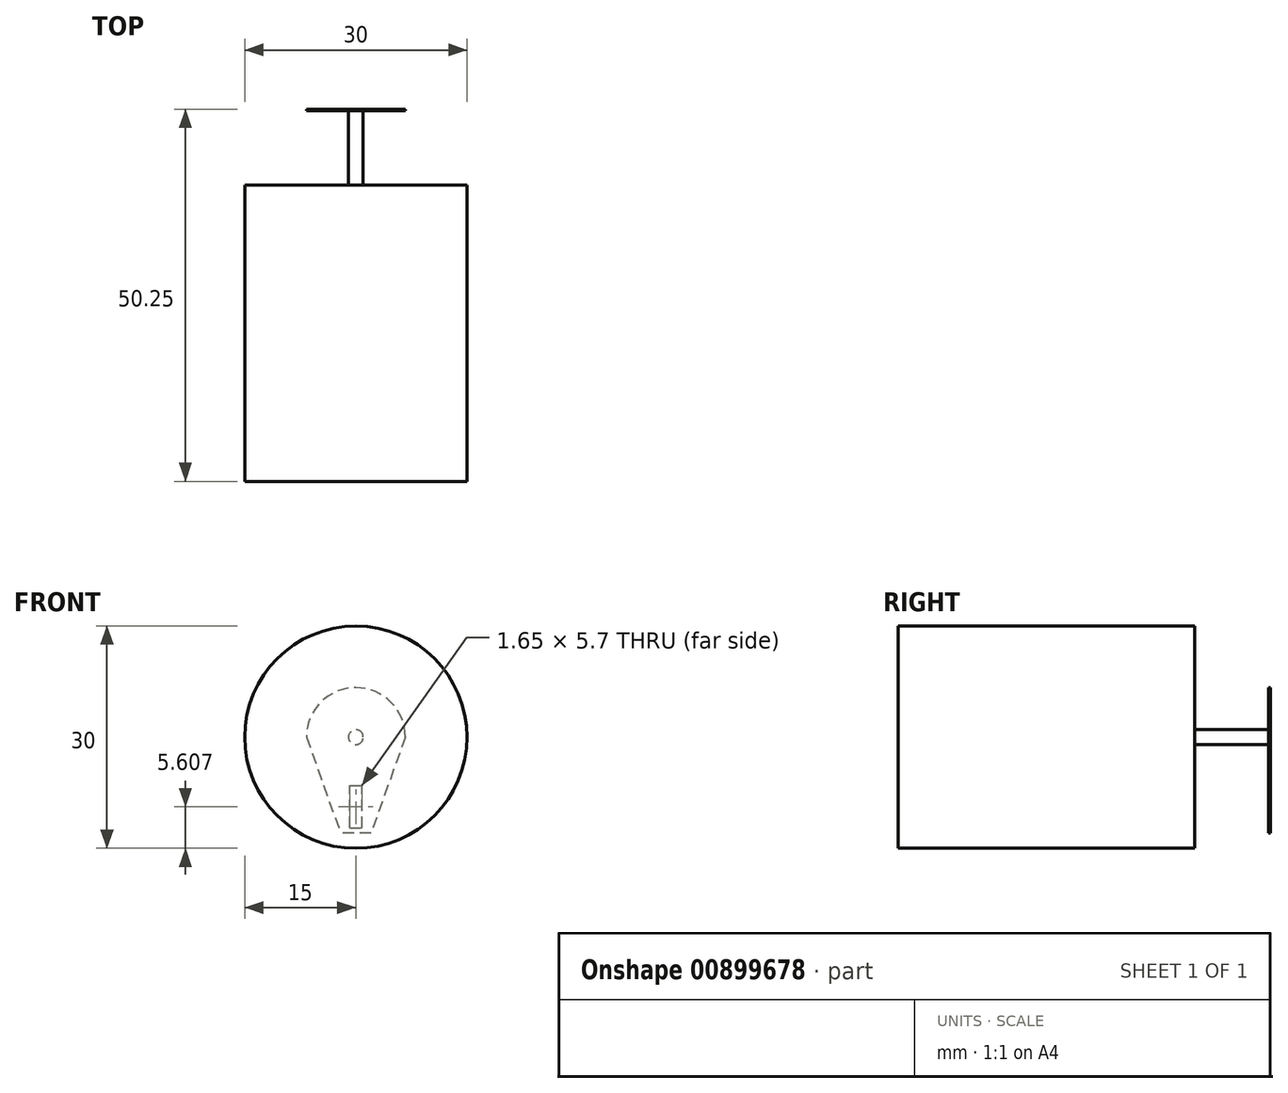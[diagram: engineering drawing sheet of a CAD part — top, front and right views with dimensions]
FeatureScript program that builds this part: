
annotation { "Feature Type Name" : "Feature", "Feature Type Description" : "" }
export const myFeature = defineFeature(function(context is Context, id is Id, definition is map)
    precondition{}
    {
        {
            var Q0;
            Q0=qCreatedBy(makeId("Front.planeOp"),FACE);
            var sketch = newSketch(context, id + "F0", { "sketchPlane" : qUnion([Q0])});
            skCircle(sketch, "E0", {"center": v(0, 0) * mm, "radius": 15 * mm});
            skSolve(sketch);
        }
        {
            var Q0;
            Q0=makeQuery(id+"F0.imprint","IMPRINT",FACE,{"disambiguationData":[TD([[makeQuery(id+"F0.imprint","IMPRINT",EDGE,{"derivedFrom":sQuery(id+"F0.wireOp",EDGE,"E0")}),1.0]])]});
            extrude(context, id + "F1", {"entities" : qUnion([Q0]), "depth" : 40 * mm, "offsetDistance" : 25.4 * mm});
        }
        {
            var Q0;
            Q0=makeQuery(id+"F1.opExtrude","CAP_FACE",FACE,{"disambiguationData":[OSD([sQuery(id+"F0.wireOp",EDGE,"E0")])],"isStart":true});
            var sketch = newSketch(context, id + "F2", { "sketchPlane" : qUnion([Q0])});
            skCircle(sketch, "E1", {"center": v(0, 0) * mm, "radius": 5 * mm});
            skCircle(sketch, "E2", {"center": v(0, 0) * mm, "radius": 1 * mm});
            skSolve(sketch);
        }
        {
            var Q0;
            Q0=makeQuery(id+"F2.imprint","IMPRINT",FACE,{"disambiguationData":[TD([[makeQuery(id+"F2.imprint","IMPRINT",EDGE,{"derivedFrom":sQuery(id+"F2.wireOp",EDGE,"E2")}),1.0]])]});
            extrude(context, id + "F3", {"entities" : qUnion([Q0]), "operationType" : NewBodyOperationType.ADD, "depth" : 10 * mm, "offsetDistance" : 25.4 * mm});
        }
        {
            var Q0;
            Q0=makeQuery(id+"F1.opExtrude","CAP_FACE",FACE,{"disambiguationData":[OSD([sQuery(id+"F0.wireOp",EDGE,"E0")])],"isStart":true});
            var sketch = newSketch(context, id + "F4", { "sketchPlane" : qUnion([Q0])});
            skSolve(sketch);
        }
        {
            var Q0;
            Q0=makeQuery(id+"F4.imprint","IMPRINT",FACE,{"disambiguationData":[TD([[makeQuery(id+"F4.imprint","IMPRINT",EDGE,{"derivedFrom":makeQuery(id+"F1.opExtrude","CAP_EDGE",EDGE,{"disambiguationData":[OSD([sQuery(id+"F0.wireOp",EDGE,"E0")])],"isStart":true})}),-1.0]])]});
            var sketch = newSketch(context, id + "F5", { "sketchPlane" : qUnion([Q0])});
            skLineSegment(sketch, "E3", {"start": v(0, -14.98) * mm, "end": v(14.98, -14.98) * mm});
            skLineSegment(sketch, "E4", {"start": v(14.98, -14.98) * mm, "end": v(-15.02, -14.98) * mm});
            skSolve(sketch);
        }
        {
            var Q0;
            Q0=sQuery(id+"F5.wireOp",EDGE,"E4");
            extrude(context, id + "F6", {"bodyType" : ToolBodyType.SURFACE, "surfaceEntities" : qUnion([Q0]), "depth" : -40 * mm, "offsetDistance" : 25.4 * mm});
        }
        {
            var Q0;
            Q0=makeQuery(id+"F3.opExtrude","CAP_FACE",FACE,{"disambiguationData":[OSD([sQuery(id+"F2.wireOp",EDGE,"E2")])],"isStart":false});
            var sketch = newSketch(context, id + "F7", { "sketchPlane" : qUnion([Q0])});
            skArc(sketch, "E5", {"start": v(6.68, 0) * mm, "mid": v(0, 6.68) * mm, "end": v(-6.68, 0) * mm, "construction": true});
            skLineSegment(sketch, "E6", {"start": v(0, -12.97) * mm, "end": v(2.03, -12.97) * mm, "construction": true});
            skLineSegment(sketch, "E7", {"start": v(0, -12.97) * mm, "end": v(-2.03, -12.97) * mm, "construction": true});
            skLineSegment(sketch, "E8", {"start": v(6.68, 0) * mm, "end": v(2.03, -12.97) * mm});
            skLineSegment(sketch, "E9", {"start": v(-6.68, 0) * mm, "end": v(-2.03, -12.97) * mm});
            skLineSegment(sketch, "E10.bottom", {"start": v(0.83, -12.24) * mm, "end": v(-0.83, -12.24) * mm});
            skLineSegment(sketch, "E10.top", {"start": v(0.83, -6.54) * mm, "end": v(-0.83, -6.54) * mm});
            skLineSegment(sketch, "E10.left", {"start": v(0.83, -12.24) * mm, "end": v(0.83, -6.54) * mm});
            skLineSegment(sketch, "E10.right", {"start": v(-0.83, -12.24) * mm, "end": v(-0.83, -6.54) * mm});
            skPoint(sketch, "E10.middle", {"position": v(0, -9.4) * mm});
            skArc(sketch, "E11", {"start": v(6.68, 0) * mm, "mid": v(0, 6.68) * mm, "end": v(-6.68, 0) * mm});
            skLineSegment(sketch, "E12", {"start": v(-2.03, -12.97) * mm, "end": v(2.03, -12.97) * mm});
            skSolve(sketch);
        }
        {
            var Q0;
            Q0 = qSketchRegion(id + "F7", true);
            extrude(context, id + "F8", {"entities" : qUnion([Q0]), "operationType" : NewBodyOperationType.ADD, "depth" : 0.25 * mm, "offsetDistance" : 25.4 * mm});
        }
    });
